# Revit family: SH-6157-18inch
name_source: partatom
category: Lighting Fixtures
revit_build: Autodesk Revit 2017 (Build: 20160225_1515(x64)
units: mm (PartAtom-declared; Revit-internal decimal feet)

## family parameters
Always vertical = Yes
Cut with Voids When Loaded = No
Host = Ceiling
Light Source = Yes
OmniClass Number = 23.80.70.11
OmniClass Title = Luminaries for Internal Lighting
Part Type = Normal
Room Calculation Point = No
Round Connector Dimension = Use Diameter
Shared = No

## types (1)
- SH-6157-18inch(White body-E27)
    Body Material = Aluminum
    Body color = White Body
    Color Filter = 16777215
    Diameter = 46 cm
    Dimming Lamp Color Temperature Shift = <None>
    Height = 46 cm
    IP = X3
    Lamp = E27
    Manufacturer = SHOA
    Model = SH-6157-18inch
    Photometric Web File = PT-150W-5000K-R80-195L-cree2835-Glass+AL cover90D_IESNA2002.IES
    Reflector Material = White Body
    Tilt Angle = 90.00°
    URL = https://www.shoaco.com
    Voltage/Frequency = 230V/50HZ
    Website = www.shoaco.com
    consumption current = 0 A
    instalation = Pendant Mounted
    wattage. = 0 W

## geometry (parser evidence)
native form markers: Sweep x1
no freeform markers — native parametric forms only
